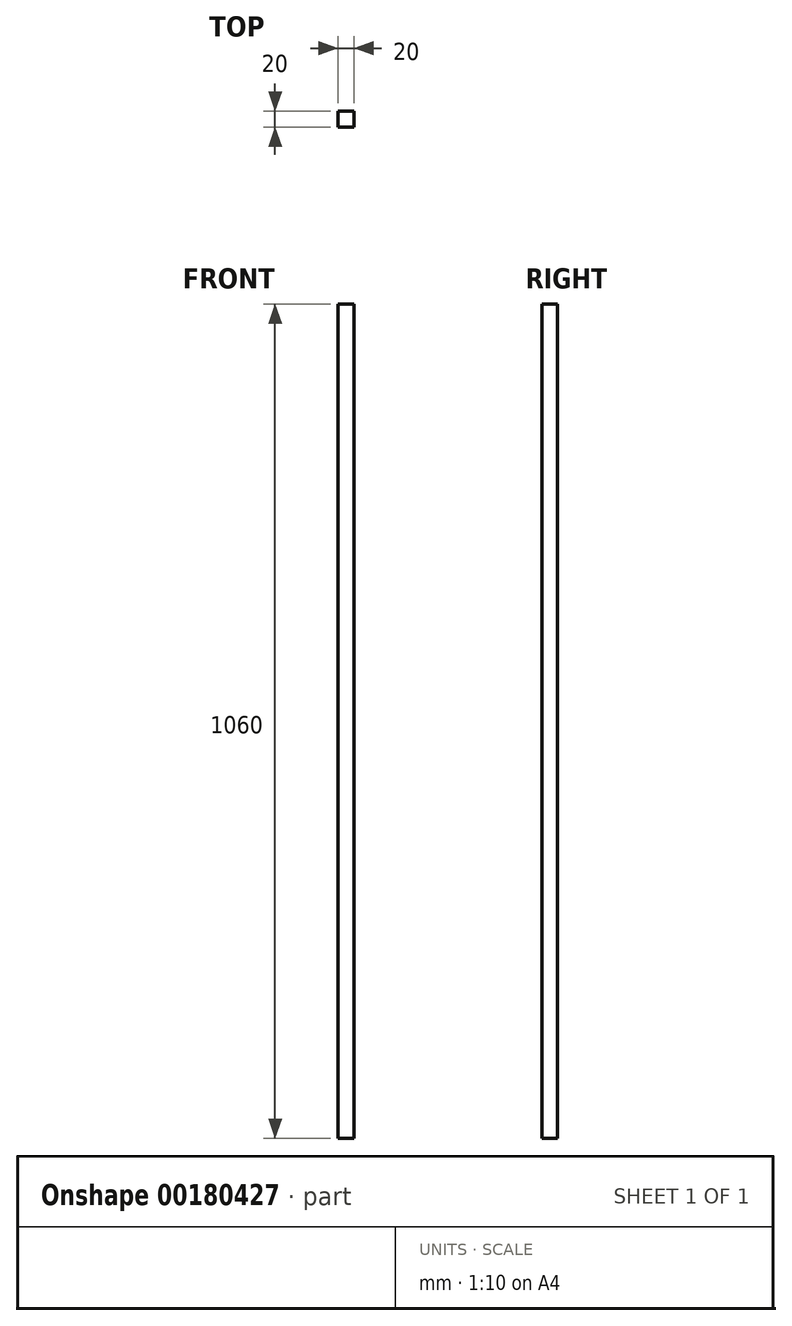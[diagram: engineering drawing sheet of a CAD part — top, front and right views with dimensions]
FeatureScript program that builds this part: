
annotation { "Feature Type Name" : "Feature", "Feature Type Description" : "" }
export const myFeature = defineFeature(function(context is Context, id is Id, definition is map)
    precondition{}
    {
        {
            var Q0;
            Q0=qCreatedBy(makeId("Top.planeOp"),FACE);
            var sketch = newSketch(context, id + "F0", { "sketchPlane" : qUnion([Q0])});
            skLineSegment(sketch, "E0.bottom", {"start": v(0, -128.62) * mm, "end": v(-20, -128.62) * mm});
            skLineSegment(sketch, "E0.top", {"start": v(0, -108.62) * mm, "end": v(-20, -108.62) * mm});
            skLineSegment(sketch, "E0.left", {"start": v(0, -128.62) * mm, "end": v(0, -108.62) * mm});
            skLineSegment(sketch, "E0.right", {"start": v(-20, -128.62) * mm, "end": v(-20, -108.62) * mm});
            skSolve(sketch);
        }
        {
            var Q0;
            Q0 = qSketchRegion(id + "F0", true);
            extrude(context, id + "F1", {"entities" : qUnion([Q0]), "depth" : 1060 * mm});
        }
    });
